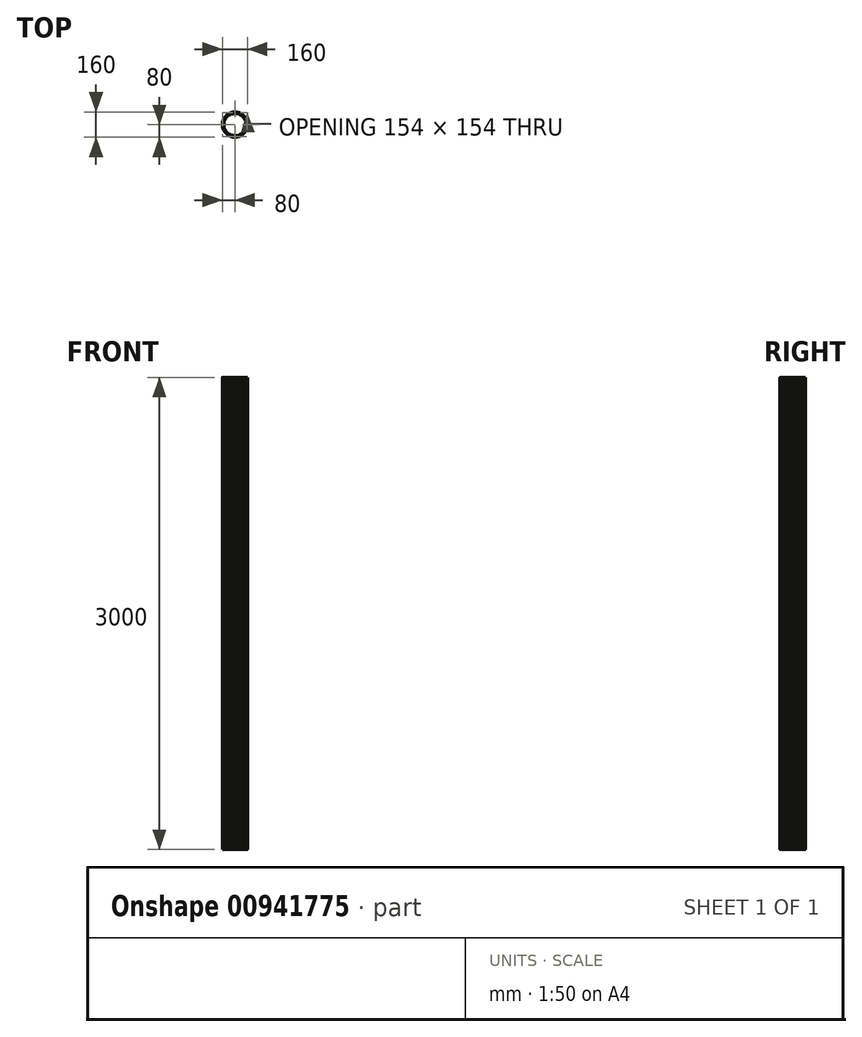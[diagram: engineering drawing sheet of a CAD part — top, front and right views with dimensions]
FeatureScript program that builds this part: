
annotation { "Feature Type Name" : "Feature", "Feature Type Description" : "" }
export const myFeature = defineFeature(function(context is Context, id is Id, definition is map)
    precondition{}
    {
        {
            var Q0;
            Q0=qCreatedBy(makeId("Top.planeOp"),FACE);
            var sketch = newSketch(context, id + "F0", { "sketchPlane" : qUnion([Q0])});
            skLineSegment(sketch, "E0", {"start": v(0, 0) * mm, "end": v(-80, 0) * mm, "construction": true});
            skArc(sketch, "E1", {"start": v(-79.3, 10.54) * mm, "mid": v(-80, 0) * mm, "end": v(-79.3, -10.54) * mm});
            skArc(sketch, "E2.0", {"start": v(-76.33, 10.14) * mm, "mid": v(-76.52, 8.61) * mm, "end": v(-76.67, 7.08) * mm});
            skArc(sketch, "E3.0", {"start": v(-72.1, 11.42) * mm, "mid": v(-72.43, 9.07) * mm, "end": v(-72.7, 6.72) * mm});
            skArc(sketch, "E4.0", {"start": v(-69.14, 10.95) * mm, "mid": v(-69.61, 7.35) * mm, "end": v(-69.9, 3.72) * mm});
            skLineSegment(sketch, "E5", {"start": v(0, 0) * mm, "end": v(-91.66, -14.52) * mm, "construction": true});
            skLineSegment(sketch, "E6.MirrorCS", {"start": v(0, 0) * mm, "end": v(-76.05, 12.05) * mm, "construction": true});
            skLineSegment(sketch, "E7", {"start": v(-76.67, -7.08) * mm, "end": v(-72.7, -6.72) * mm});
            skLineSegment(sketch, "E8.MirrorCS", {"start": v(-76.67, 7.08) * mm, "end": v(-72.7, 6.72) * mm});
            skLineSegment(sketch, "E9", {"start": v(-79.02, 12.51) * mm, "end": v(-76.05, 12.05) * mm});
            skPoint(sketch, "E10.orphan", {"position": v(-89.94, 8.3) * mm});
            skPoint(sketch, "E11.orphan", {"position": v(-89.94, -8.3) * mm});
            skLineSegment(sketch, "E12", {"start": v(-76.9, 4.1) * mm, "end": v(-69.9, 3.72) * mm});
            skLineSegment(sketch, "E13.MirrorCS", {"start": v(-76.9, -4.1) * mm, "end": v(-69.9, -3.72) * mm});
            skLineSegment(sketch, "E14", {"start": v(-79.3, 10.54) * mm, "end": v(-76.33, 10.14) * mm});
            skLineSegment(sketch, "E15.trimOffspring", {"start": v(-79.02, 12.51) * mm, "end": v(-91.66, 14.52) * mm, "construction": true});
            skLineSegment(sketch, "E16.MirrorCS", {"start": v(-79.3, -10.54) * mm, "end": v(-76.33, -10.14) * mm});
            skArc(sketch, "E17.trimOffspring", {"start": v(-72.7, -6.72) * mm, "mid": v(-72.43, -9.07) * mm, "end": v(-72.1, -11.42) * mm});
            skArc(sketch, "E18.trimOffspring", {"start": v(-76.67, -7.08) * mm, "mid": v(-76.52, -8.61) * mm, "end": v(-76.33, -10.14) * mm});
            skArc(sketch, "E19.trimOffspring", {"start": v(-76.9, 4.1) * mm, "mid": v(-77, 0) * mm, "end": v(-76.9, -4.1) * mm});
            skArc(sketch, "E20.trimOffspring", {"start": v(-69.9, -3.72) * mm, "mid": v(-69.61, -7.35) * mm, "end": v(-69.14, -10.95) * mm});
            skLineSegment(sketch, "E21", {"start": v(-72.1, 11.42) * mm, "end": v(-69.14, 10.95) * mm});
            skLineSegment(sketch, "E22", {"start": v(-72.1, -11.42) * mm, "end": v(-69.14, -10.95) * mm});
            skSolve(sketch);
        }
        {
            var Q0;
            Q0 = qSketchRegion(id + "F0", true);
            extrude(context, id + "F1", {"entities" : qUnion([Q0]), "depth" : 3000 * mm, "offsetDistance" : 25 * mm});
        }
        {
            var Q0;
            Q0=makeQuery(id+"F1.opExtrude","SWEPT_EDGE",EDGE,{"disambiguationData":[OSD([sQuery(id+"F0.wireOp",EDGE,"E1"),sQuery(id+"F0.wireOp",EDGE,"E14")])]});
            var Q1;
            Q1=makeQuery(id+"F1.opExtrude","SWEPT_EDGE",EDGE,{"disambiguationData":[OSD([sQuery(id+"F0.wireOp",EDGE,"E1"),sQuery(id+"F0.wireOp",EDGE,"E16.MirrorCS")])]});
            var Q2;
            Q2=makeQuery(id+"F1.opExtrude","SWEPT_EDGE",EDGE,{"disambiguationData":[OSD([sQuery(id+"F0.wireOp",EDGE,"E16.MirrorCS"),sQuery(id+"F0.wireOp",EDGE,"E18.trimOffspring")])]});
            var Q3;
            Q3=makeQuery(id+"F1.opExtrude","SWEPT_EDGE",EDGE,{"disambiguationData":[OSD([sQuery(id+"F0.wireOp",EDGE,"E7"),sQuery(id+"F0.wireOp",EDGE,"E18.trimOffspring")])]});
            var Q4;
            Q4=makeQuery(id+"F1.opExtrude","SWEPT_EDGE",EDGE,{"disambiguationData":[OSD([sQuery(id+"F0.wireOp",EDGE,"E7"),sQuery(id+"F0.wireOp",EDGE,"E17.trimOffspring")])]});
            var Q5;
            Q5=makeQuery(id+"F1.opExtrude","SWEPT_EDGE",EDGE,{"disambiguationData":[OSD([sQuery(id+"F0.wireOp",EDGE,"E2.0"),sQuery(id+"F0.wireOp",EDGE,"E14")])]});
            var Q6;
            Q6=makeQuery(id+"F1.opExtrude","SWEPT_EDGE",EDGE,{"disambiguationData":[OSD([sQuery(id+"F0.wireOp",EDGE,"E3.0"),sQuery(id+"F0.wireOp",EDGE,"E8.MirrorCS")])]});
            var Q7;
            Q7=makeQuery(id+"F1.opExtrude","SWEPT_EDGE",EDGE,{"disambiguationData":[OSD([sQuery(id+"F0.wireOp",EDGE,"E2.0"),sQuery(id+"F0.wireOp",EDGE,"E8.MirrorCS")])]});
            var Q8;
            Q8=makeQuery(id+"F1.opExtrude","SWEPT_EDGE",EDGE,{"disambiguationData":[OSD([sQuery(id+"F0.wireOp",EDGE,"E13.MirrorCS"),sQuery(id+"F0.wireOp",EDGE,"E20.trimOffspring")])]});
            var Q9;
            Q9=makeQuery(id+"F1.opExtrude","SWEPT_EDGE",EDGE,{"disambiguationData":[OSD([sQuery(id+"F0.wireOp",EDGE,"E4.0"),sQuery(id+"F0.wireOp",EDGE,"E12")])]});
            var Q10;
            Q10=makeQuery(id+"F1.opExtrude","SWEPT_EDGE",EDGE,{"disambiguationData":[OSD([sQuery(id+"F0.wireOp",EDGE,"E13.MirrorCS"),sQuery(id+"F0.wireOp",EDGE,"E19.trimOffspring")])]});
            var Q11;
            Q11=makeQuery(id+"F1.opExtrude","SWEPT_EDGE",EDGE,{"disambiguationData":[OSD([sQuery(id+"F0.wireOp",EDGE,"E12"),sQuery(id+"F0.wireOp",EDGE,"E19.trimOffspring")])]});
            fillet(context, id + "F2", {"entities" : qUnion([Q0, Q1, Q2, Q3, Q4, Q5, Q6, Q7, Q8, Q9, Q10, Q11]), "radius" : 1 * mm, "tangentPropagation" : true, "allowEdgeOverflow" : false});
        }
        {
            var Q0;
            Q0=qCreatedBy(makeId("Front.planeOp"),FACE);
            var sketch = newSketch(context, id + "F3", { "sketchPlane" : qUnion([Q0])});
            skLineSegment(sketch, "E23", {"start": v(0, -14.54) * mm, "end": v(0, 781.55) * mm, "construction": true});
            skSolve(sketch);
        }
        {
            var Q0;
            Q0=makeQuery(id+"F1.opExtrude","SWEPT_BODY",BODY,{"disambiguationData":[OSD([sQuery(id+"F0.wireOp",EDGE,"E1"),sQuery(id+"F0.wireOp",EDGE,"E2.0"),sQuery(id+"F0.wireOp",EDGE,"E3.0"),sQuery(id+"F0.wireOp",EDGE,"E4.0"),sQuery(id+"F0.wireOp",EDGE,"E7"),sQuery(id+"F0.wireOp",EDGE,"E8.MirrorCS"),sQuery(id+"F0.wireOp",EDGE,"E12"),sQuery(id+"F0.wireOp",EDGE,"E13.MirrorCS"),sQuery(id+"F0.wireOp",EDGE,"E14"),sQuery(id+"F0.wireOp",EDGE,"E16.MirrorCS"),sQuery(id+"F0.wireOp",EDGE,"E17.trimOffspring"),sQuery(id+"F0.wireOp",EDGE,"E18.trimOffspring"),sQuery(id+"F0.wireOp",EDGE,"E19.trimOffspring"),sQuery(id+"F0.wireOp",EDGE,"E20.trimOffspring"),sQuery(id+"F0.wireOp",EDGE,"E21"),sQuery(id+"F0.wireOp",EDGE,"E22")])]});
            var Q1;
            Q1=sQuery(id+"F3.wireOp",EDGE,"E23");
            circularPattern(context, id + "F4", {"operationType" : NewBodyOperationType.ADD, "entities" : qUnion([Q0]), "axis" : qUnion([Q1]), "angle" : 360 * degree, "instanceCount" : 20, "equalSpace" : true});
        }
    });
